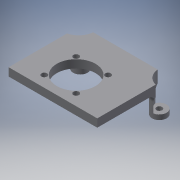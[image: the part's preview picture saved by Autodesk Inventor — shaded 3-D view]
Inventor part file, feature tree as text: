
AUTODESK INVENTOR PART (.ipt)
format: ipt  version: 2016 (Build 200138000, 138)  size: 232,448 bytes
history: native  units: mm
features: sketch x7, extrude x6, projected_geometry x5, mirror x2, fillet x1, hole x1
ambient origin geometry x8: Origin, YZ Plane, XZ Plane, XY Plane, X Axis, Y Axis, Z Axis, Center Point
bodies: Solid1 (feature_tree)
feature tree (22):
  extrude  "Extrusion1"  Depth=45.0mm
  extrude  "Extrusion2"  Depth=30.0mm TaperAngle=0.0deg
  extrude  "Extrusion4"  Depth=6.0mm
  extrude  "Extrusion5"  Depth=27.0mm TaperAngle=0.0deg
  mirror  "Mirror2"
  fillet  "Fillet1"  Radius=3.5mm
  mirror  "Mirror3"
  extrude  "Extrusion6"  Depth=49.0mm
  hole  "Hole2"  [1 undecoded]
  extrude  "Extrusion7"  Depth=25.0mm TaperAngle=0.0deg
  sketch  "Sketch1"  dims[d0=55.0mm d1=45.0mm]
  sketch  "Sketch2"  dims[d2=5.0mm d3=0.0mm d6=30.0mm d7=0.0mm]
  projected_geometry  "Projected Loop1"
  sketch  "Sketch3"  dims[d11=6.0mm d19=9.0mm]
  projected_geometry  "Projected Loop2"
  sketch  "Sketch5"  dims[d20=9.0mm d25=27.0mm d26=0.0mm d27=3.5mm]
  projected_geometry  "Projected Loop4"
  sketch  "Sketch6"  dims[d28=17.0mm d29=0.0mm d30=49.0mm]
  sketch  "Sketch7"  dims[d31=3.5mm d32=6.0mm]
  projected_geometry  "Projected Loop5"
  sketch  "Sketch8"  dims[d33=24.0mm d34=17.0mm d35=0.0mm d36=28.0mm d37=45.0deg d38=40.0mm d40=360.0deg d42=3.5mm d43=6.0mm d44=4.0mm d45=2.0mm d46=90.0deg d47=8.0mm d48=20.594885mm d49=6.0mm d50=6.0mm d51=25.0mm d52=0.0mm]
  projected_geometry  "Projected Loop6"
note: 1 required parameter value undecoded (feature->parameter linkage not recoverable at this tier; creation-order binding heuristic only, values carry confidence <= 0.55)
